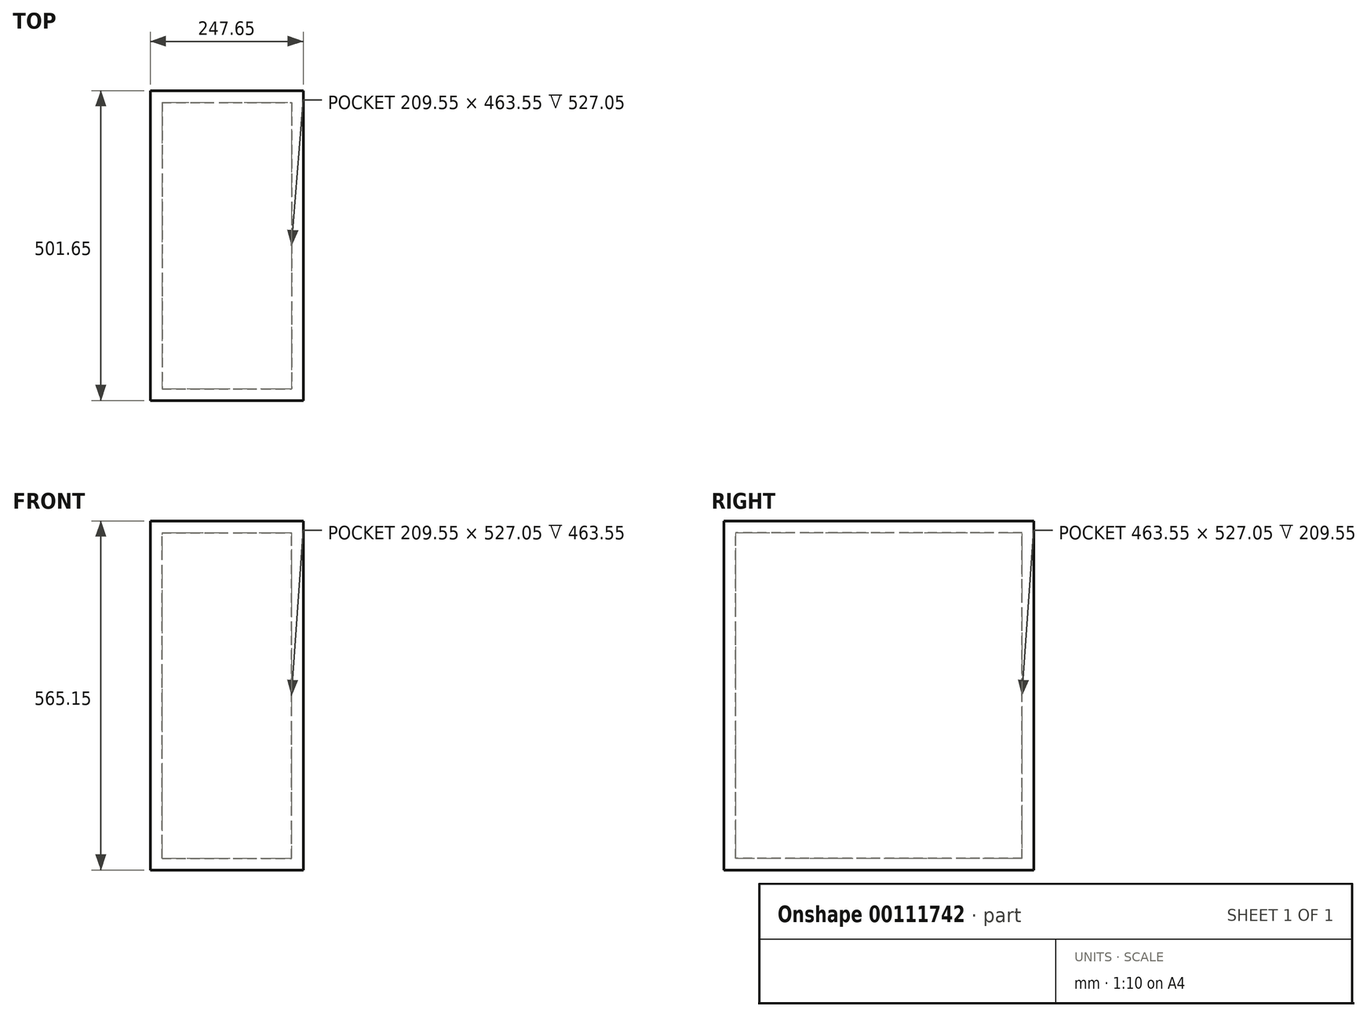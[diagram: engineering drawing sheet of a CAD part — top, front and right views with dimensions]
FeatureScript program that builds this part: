
annotation { "Feature Type Name" : "Feature", "Feature Type Description" : "" }
export const myFeature = defineFeature(function(context is Context, id is Id, definition is map)
    precondition{}
    {
        {
            var Q0;
            Q0=qCreatedBy(makeId("Top.planeOp"),FACE);
            var sketch = newSketch(context, id + "F0", { "sketchPlane" : qUnion([Q0])});
            skLineSegment(sketch, "E0.bottom", {"start": v(-206.18, 444.6) * mm, "end": v(41.47, 444.6) * mm});
            skLineSegment(sketch, "E0.top", {"start": v(-206.18, -57.05) * mm, "end": v(41.47, -57.05) * mm});
            skLineSegment(sketch, "E0.left", {"start": v(-206.18, 444.6) * mm, "end": v(-206.18, -57.05) * mm});
            skLineSegment(sketch, "E0.right", {"start": v(41.47, 444.6) * mm, "end": v(41.47, -57.05) * mm});
            skSolve(sketch);
        }
        {
            var Q0;
            Q0=makeQuery(id+"F0.imprint","IMPRINT",FACE,{"disambiguationData":[TD([[makeQuery(id+"F0.imprint","IMPRINT",EDGE,{"derivedFrom":sQuery(id+"F0.wireOp",EDGE,"E0.bottom")}),-1.0]])]});
            extrude(context, id + "F1", {"entities" : qUnion([Q0]), "depth" : 19.05 * mm});
        }
        {
            var Q0;
            Q0=makeQuery(id+"F1.opExtrude","CAP_FACE",FACE,{"disambiguationData":[OSD([sQuery(id+"F0.wireOp",EDGE,"E0.bottom"),sQuery(id+"F0.wireOp",EDGE,"E0.top"),sQuery(id+"F0.wireOp",EDGE,"E0.left"),sQuery(id+"F0.wireOp",EDGE,"E0.right")])],"isStart":true});
            var sketch = newSketch(context, id + "F2", { "sketchPlane" : qUnion([Q0])});
            skLineSegment(sketch, "E1.bottom", {"start": v(-187.13, -425.55) * mm, "end": v(22.42, -425.55) * mm});
            skLineSegment(sketch, "E1.top", {"start": v(-187.13, 38) * mm, "end": v(22.42, 38) * mm});
            skLineSegment(sketch, "E1.left", {"start": v(-187.13, -425.55) * mm, "end": v(-187.13, 38) * mm});
            skLineSegment(sketch, "E1.right", {"start": v(22.42, -425.55) * mm, "end": v(22.42, 38) * mm});
            skSolve(sketch);
        }
        {
            var Q0;
            Q0=makeQuery(id+"F2.imprint","IMPRINT",FACE,{"disambiguationData":[TD([[makeQuery(id+"F2.imprint","IMPRINT",EDGE,{"derivedFrom":sQuery(id+"F2.wireOp",EDGE,"E1.bottom")}),-1.0]])]});
            extrude(context, id + "F3", {"entities" : qUnion([Q0]), "operationType" : NewBodyOperationType.ADD, "depth" : 546.1 * mm});
        }
        {
            var Q0;
            {var subQ0=sQuery(id+"F0.wireOp",EDGE,"E0.left");Q0=makeQuery(id+"F3.boolean.opBoolean","MERGE",FACE,{"derivedFrom":[makeQuery(id+"F1.opExtrude","SWEPT_FACE",FACE,{"disambiguationData":[OSD([subQ0])]}),makeQuery(id+"F3.opExtrude","SWEPT_FACE",FACE,{"disambiguationData":[OSD([subQ0])]})]});}
            var sketch = newSketch(context, id + "F4", { "sketchPlane" : qUnion([Q0])});
            skLineSegment(sketch, "E2.bottom", {"start": v(-444.6, -546.1) * mm, "end": v(57.05, -546.1) * mm});
            skLineSegment(sketch, "E2.top", {"start": v(-444.6, -527.05) * mm, "end": v(57.05, -527.05) * mm});
            skLineSegment(sketch, "E2.left", {"start": v(-444.6, -546.1) * mm, "end": v(-444.6, -527.05) * mm});
            skLineSegment(sketch, "E2.right", {"start": v(57.05, -546.1) * mm, "end": v(57.05, -527.05) * mm});
            skSolve(sketch);
        }
        {
            var Q0;
            Q0=makeQuery(id+"F4.imprint","IMPRINT",FACE,{"disambiguationData":[TD([[makeQuery(id+"F4.imprint","IMPRINT",EDGE,{"derivedFrom":sQuery(id+"F4.wireOp",EDGE,"E2.bottom")}),1.0]])]});
            extrude(context, id + "F5", {"entities" : qUnion([Q0]), "operationType" : NewBodyOperationType.ADD, "oppositeDirection" : true, "depth" : 247.65 * mm});
        }
    });
